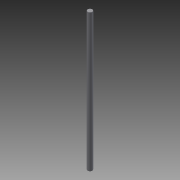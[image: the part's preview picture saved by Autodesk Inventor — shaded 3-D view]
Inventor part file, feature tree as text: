
AUTODESK INVENTOR PART (.ipt)
format: ipt  version: 2015 SP1 (Build 190203100, 203)  size: 64,000 bytes
history: native  units: mm
features: other x3, sketch x1
ambient origin geometry x8: Origin, YZ Plane, XZ Plane, XY Plane, X Axis, Y Axis, Z Axis, Center Point
bodies: Solid1 (feature_tree)
feature tree (4):
  other  "tige.ipt"
  other  "Solid1::tige.ipt"
  other  "TaggingFeature1"
  sketch  "Sketch1"  dims[d0=10.0mm]
